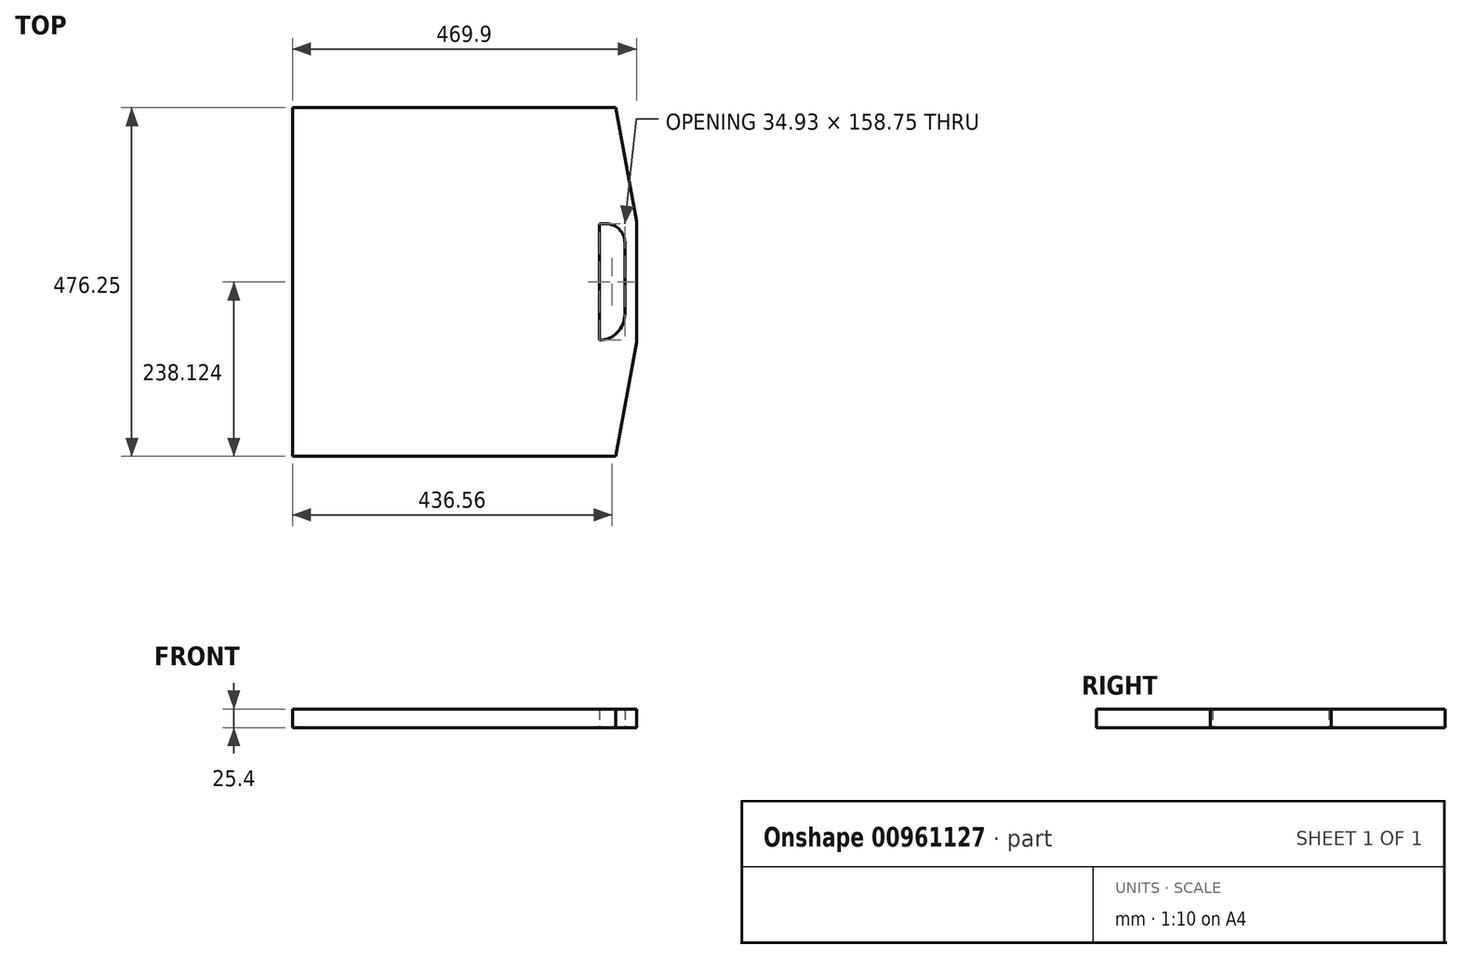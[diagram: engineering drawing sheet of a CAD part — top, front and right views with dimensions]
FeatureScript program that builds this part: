
annotation { "Feature Type Name" : "Feature", "Feature Type Description" : "" }
export const myFeature = defineFeature(function(context is Context, id is Id, definition is map)
    precondition{}
    {
        {
            var Q0;
            Q0=qCreatedBy(makeId("Top.planeOp"),FACE);
            var sketch = newSketch(context, id + "F0", { "sketchPlane" : qUnion([Q0])});
            skLineSegment(sketch, "E0.bottom", {"start": v(72.83, -177.44) * mm, "end": v(-368.5, -177.44) * mm});
            skLineSegment(sketch, "E0.top", {"start": v(72.83, 298.8) * mm, "end": v(-368.5, 298.8) * mm});
            skLineSegment(sketch, "E0.left", {"start": v(72.83, -177.44) * mm, "end": v(72.83, 298.8) * mm});
            skLineSegment(sketch, "E0.right", {"start": v(-368.5, -177.44) * mm, "end": v(-368.5, 298.8) * mm});
            skPoint(sketch, "E0.middle", {"position": v(-147.83, 60.68) * mm});
            skLineSegment(sketch, "E1.bottom", {"start": v(72.83, 143.23) * mm, "end": v(101.4, 143.23) * mm});
            skLineSegment(sketch, "E1.top", {"start": v(72.83, -21.87) * mm, "end": v(101.4, -21.87) * mm});
            skLineSegment(sketch, "E1.left", {"start": v(72.83, 143.23) * mm, "end": v(72.83, -21.87) * mm});
            skLineSegment(sketch, "E1.right", {"start": v(101.4, 143.23) * mm, "end": v(101.4, -21.87) * mm});
            skLineSegment(sketch, "E2", {"start": v(72.83, -177.44) * mm, "end": v(101.4, -21.87) * mm});
            skLineSegment(sketch, "E3", {"start": v(72.83, 298.8) * mm, "end": v(101.4, 143.23) * mm});
            skLineSegment(sketch, "E4.bottom", {"start": v(50.6, 140.06) * mm, "end": v(60.13, 140.06) * mm});
            skLineSegment(sketch, "E4.top", {"start": v(50.6, -18.7) * mm, "end": v(50.6, -18.7) * mm});
            skLineSegment(sketch, "E4.left", {"start": v(50.6, 140.06) * mm, "end": v(50.6, -18.7) * mm});
            skLineSegment(sketch, "E4.right", {"start": v(85.53, 114.66) * mm, "end": v(85.53, 16.23) * mm});
            skPoint(sketch, "E5.visualSharp", {"position": v(85.53, 140.06) * mm});
            skArc(sketch, "E5.filletArc", {"start": v(85.53, 114.66) * mm, "mid": v(78.1, 132.62) * mm, "end": v(60.13, 140.06) * mm});
            skPoint(sketch, "E6.visualSharp", {"position": v(85.53, -18.7) * mm});
            skArc(sketch, "E6.filletArc", {"start": v(50.6, -18.7) * mm, "mid": v(75.3, -8.46) * mm, "end": v(85.53, 16.23) * mm});
            skSolve(sketch);
        }
        {
            var Q0;
            {var subQ0=sQuery(id+"F0.wireOp",EDGE,"E1.top");var subQ1=makeQuery(id+"F0.imprint","IMPRINT",EDGE,{"derivedFrom":subQ0});var subQ2=sQuery(id+"F0.wireOp",EDGE,"E1.bottom");var subQ3=makeQuery(id+"F0.imprint","IMPRINT",EDGE,{"derivedFrom":subQ2});var subQ15=sQuery(id+"F0.wireOp",EDGE,"E0.bottom");Q0=qUnion([makeQuery(id+"F0.imprint","IMPRINT",FACE,{"disambiguationData":[TD([[subQ1,-1.0]])]}),makeQuery(id+"F0.imprint","IMPRINT",FACE,{"disambiguationData":[TD([[subQ3,1.0]])]}),makeQuery(id+"F0.imprint","IMPRINT",FACE,{"disambiguationData":[TD([[makeQuery(id+"F0.imprint","IMPRINT",EDGE,{"derivedFrom":subQ15}),-1.0]])]}),makeQuery(id+"F0.imprint","IMPRINT",FACE,{"disambiguationData":[TD([[subQ3,-1.0]])]})]);}
            extrude(context, id + "F1", {"entities" : qUnion([Q0]), "depth" : 25.4 * mm, "offsetDistance" : 25.4 * mm});
        }
    });
